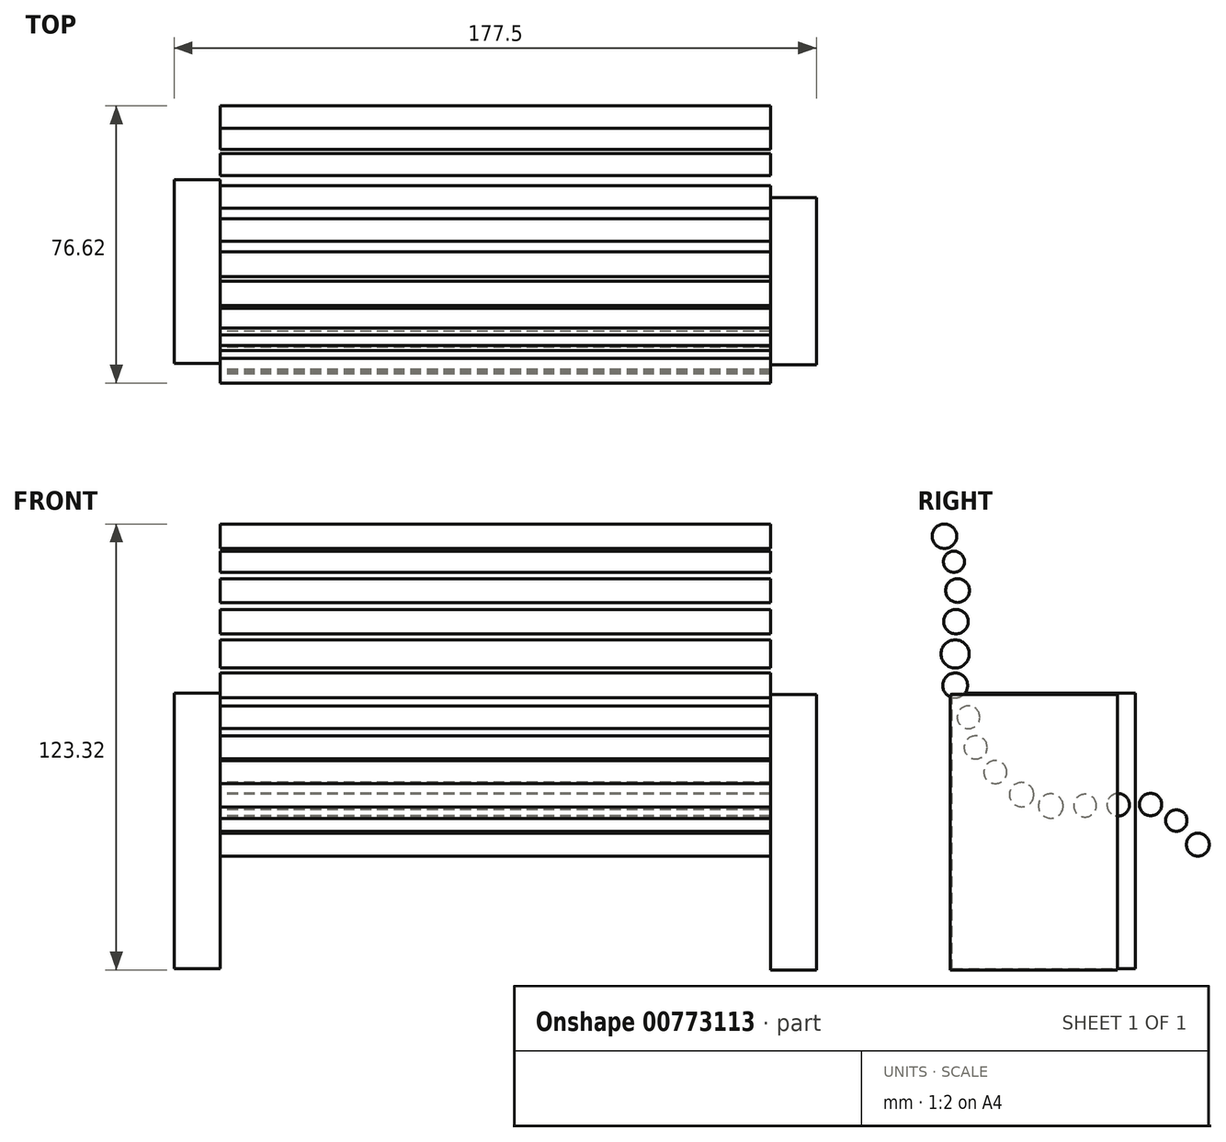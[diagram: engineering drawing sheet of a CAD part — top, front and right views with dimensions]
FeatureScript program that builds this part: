
annotation { "Feature Type Name" : "Feature", "Feature Type Description" : "" }
export const myFeature = defineFeature(function(context is Context, id is Id, definition is map)
    precondition{}
    {
        {
            var Q0;
            Q0=qCreatedBy(makeId("Right.planeOp"),FACE);
            var sketch = newSketch(context, id + "F0", { "sketchPlane" : qUnion([Q0])});
            skCircle(sketch, "E0", {"center": v(45.38, -24.06) * mm, "radius": 3.16 * mm});
            skPoint(sketch, "E0.first.point", {"position": v(47.49, -26.42) * mm});
            skPoint(sketch, "E0.second.point", {"position": v(45.04, -20.92) * mm});
            skPoint(sketch, "E0.third.point", {"position": v(42.3, -23.36) * mm});
            skCircle(sketch, "E1", {"center": v(39.43, -17.41) * mm, "radius": 2.97 * mm});
            skPoint(sketch, "E1.first.point", {"position": v(42.3, -18.17) * mm});
            skPoint(sketch, "E1.second.point", {"position": v(36.5, -17.86) * mm});
            skPoint(sketch, "E1.third.point", {"position": v(36.8, -16.03) * mm});
            skCircle(sketch, "E2", {"center": v(32.3, -12.98) * mm, "radius": 3.1 * mm});
            skPoint(sketch, "E2.first.point", {"position": v(32.83, -16.03) * mm});
            skPoint(sketch, "E2.second.point", {"position": v(33.74, -10.23) * mm});
            skPoint(sketch, "E2.third.point", {"position": v(30.39, -10.54) * mm});
            skCircle(sketch, "E3", {"center": v(23.36, -13.06) * mm, "radius": 3.12 * mm});
            skPoint(sketch, "E3.first.point", {"position": v(24.28, -16.03) * mm});
            skPoint(sketch, "E3.second.point", {"position": v(25.2, -10.54) * mm});
            skPoint(sketch, "E3.third.point", {"position": v(21.53, -10.54) * mm});
            skCircle(sketch, "E4", {"center": v(14.2, -13.28) * mm, "radius": 3.14 * mm});
            skPoint(sketch, "E4.first.point", {"position": v(15.73, -16.03) * mm});
            skPoint(sketch, "E4.second.point", {"position": v(15.73, -10.54) * mm});
            skPoint(sketch, "E4.third.point", {"position": v(12.67, -10.54) * mm});
            skCircle(sketch, "E5", {"center": v(4.73, -13.4) * mm, "radius": 3.4 * mm});
            skPoint(sketch, "E5.first.point", {"position": v(6.87, -16.03) * mm});
            skPoint(sketch, "E5.second.point", {"position": v(6.57, -10.54) * mm});
            skPoint(sketch, "E5.third.point", {"position": v(2.9, -10.54) * mm});
            skCircle(sketch, "E6", {"center": v(-3.36, -10.25) * mm, "radius": 3.37 * mm});
            skPoint(sketch, "E6.first.point", {"position": v(-2.9, -13.59) * mm});
            skPoint(sketch, "E6.second.point", {"position": v(0, -10.54) * mm});
            skPoint(sketch, "E6.third.point", {"position": v(-5.95, -8.1) * mm});
            skCircle(sketch, "E7", {"center": v(-10.62, -4.02) * mm, "radius": 3.18 * mm});
            skPoint(sketch, "E7.first.point", {"position": v(-10.23, -7.18) * mm});
            skPoint(sketch, "E7.second.point", {"position": v(-7.48, -3.51) * mm});
            skPoint(sketch, "E7.third.point", {"position": v(-13.28, -2.3) * mm});
            skCircle(sketch, "E8", {"center": v(-16.03, 2.8) * mm, "radius": 3.2 * mm});
            skPoint(sketch, "E8.first.point", {"position": v(-17.56, 0) * mm});
            skPoint(sketch, "E8.second.point", {"position": v(-18.78, 4.43) * mm});
            skPoint(sketch, "E8.third.point", {"position": v(-13.28, 4.43) * mm});
            skCircle(sketch, "E9", {"center": v(-18.02, 11.15) * mm, "radius": 3.15 * mm});
            skPoint(sketch, "E9.first.point", {"position": v(-16.03, 8.7) * mm});
            skPoint(sketch, "E9.second.point", {"position": v(-18.78, 8.1) * mm});
            skPoint(sketch, "E9.third.point", {"position": v(-18.78, 14.2) * mm});
            skCircle(sketch, "E10", {"center": v(-21.71, 19.96) * mm, "radius": 3.43 * mm});
            skPoint(sketch, "E10.first.point", {"position": v(-18.78, 18.17) * mm});
            skPoint(sketch, "E10.second.point", {"position": v(-23.36, 16.95) * mm});
            skPoint(sketch, "E10.third.point", {"position": v(-22.14, 23.36) * mm});
            skCircle(sketch, "E11", {"center": v(-21.71, 28.67) * mm, "radius": 3.9 * mm});
            skPoint(sketch, "E11.first.point", {"position": v(-18.78, 26.11) * mm});
            skPoint(sketch, "E11.second.point", {"position": v(-24.89, 26.42) * mm});
            skPoint(sketch, "E11.third.point", {"position": v(-24.58, 31.3) * mm});
            skCircle(sketch, "E12", {"center": v(-21.5, 37.6) * mm, "radius": 3.4 * mm});
            skPoint(sketch, "E12.first.point", {"position": v(-18.78, 35.58) * mm});
            skPoint(sketch, "E12.second.point", {"position": v(-24.89, 37.71) * mm});
            skPoint(sketch, "E12.third.point", {"position": v(-24.28, 39.55) * mm});
            skCircle(sketch, "E13", {"center": v(-21.06, 46.2) * mm, "radius": 3.29 * mm});
            skPoint(sketch, "E13.first.point", {"position": v(-18.78, 43.82) * mm});
            skPoint(sketch, "E13.second.point", {"position": v(-24.28, 46.88) * mm});
            skPoint(sketch, "E13.third.point", {"position": v(-22.75, 49.01) * mm});
            skCircle(sketch, "E14", {"center": v(-22.05, 54.16) * mm, "radius": 2.91 * mm});
            skPoint(sketch, "E14.first.point", {"position": v(-19.4, 52.98) * mm});
            skPoint(sketch, "E14.second.point", {"position": v(-24.28, 56.04) * mm});
            skPoint(sketch, "E14.third.point", {"position": v(-24.89, 54.82) * mm});
            skCircle(sketch, "E15", {"center": v(-24.69, 61.22) * mm, "radius": 3.4 * mm});
            skPoint(sketch, "E15.first.point", {"position": v(-27.33, 59.1) * mm});
            skPoint(sketch, "E15.second.point", {"position": v(-24.28, 64.59) * mm});
            skPoint(sketch, "E15.third.point", {"position": v(-21.83, 63.06) * mm});
            skSolve(sketch);
        }
        {
            var Q0;
            Q0 = qSketchRegion(id + "F0", true);
            extrude(context, id + "F1", {"entities" : qUnion([Q0]), "depth" : 152.15 * mm, "offsetDistance" : 25.4 * mm});
        }
        {
            var Q0;
            Q0=qCreatedBy(makeId("Right.planeOp"),FACE);
            var sketch = newSketch(context, id + "F2", { "sketchPlane" : qUnion([Q0])});
            skLineSegment(sketch, "E16.bottom", {"start": v(-22.65, 17.8) * mm, "end": v(28.15, 17.8) * mm});
            skLineSegment(sketch, "E16.top", {"start": v(-22.65, -58.4) * mm, "end": v(28.15, -58.4) * mm});
            skLineSegment(sketch, "E16.left", {"start": v(-22.65, 17.8) * mm, "end": v(-22.65, -58.4) * mm});
            skLineSegment(sketch, "E16.right", {"start": v(28.15, 17.8) * mm, "end": v(28.15, -58.4) * mm});
            skSolve(sketch);
        }
        {
            var Q0;
            Q0 = qSketchRegion(id + "F2", true);
            extrude(context, id + "F3", {"entities" : qUnion([Q0]), "oppositeDirection" : true, "depth" : 12.7 * mm, "offsetDistance" : 25.4 * mm});
        }
        {
            var Q0;
            Q0=qCreatedBy(makeId("Front.planeOp"),FACE);
            var sketch = newSketch(context, id + "F4", { "sketchPlane" : qUnion([Q0])});
            skLineSegment(sketch, "E17.bottom", {"start": v(152.1, 17.49) * mm, "end": v(164.8, 17.49) * mm});
            skLineSegment(sketch, "E17.top", {"start": v(152.1, -58.71) * mm, "end": v(164.8, -58.71) * mm});
            skLineSegment(sketch, "E17.left", {"start": v(152.1, 17.49) * mm, "end": v(152.1, -58.71) * mm});
            skLineSegment(sketch, "E17.right", {"start": v(164.8, 17.49) * mm, "end": v(164.8, -58.71) * mm});
            skSolve(sketch);
        }
        {
            var Q0;
            Q0 = qSketchRegion(id + "F4", true);
            extrude(context, id + "F5", {"entities" : qUnion([Q0]), "endBound" : BoundingType.SYMMETRIC, "depth" : 46.23 * mm, "offsetDistance" : 25.4 * mm});
        }
    });
